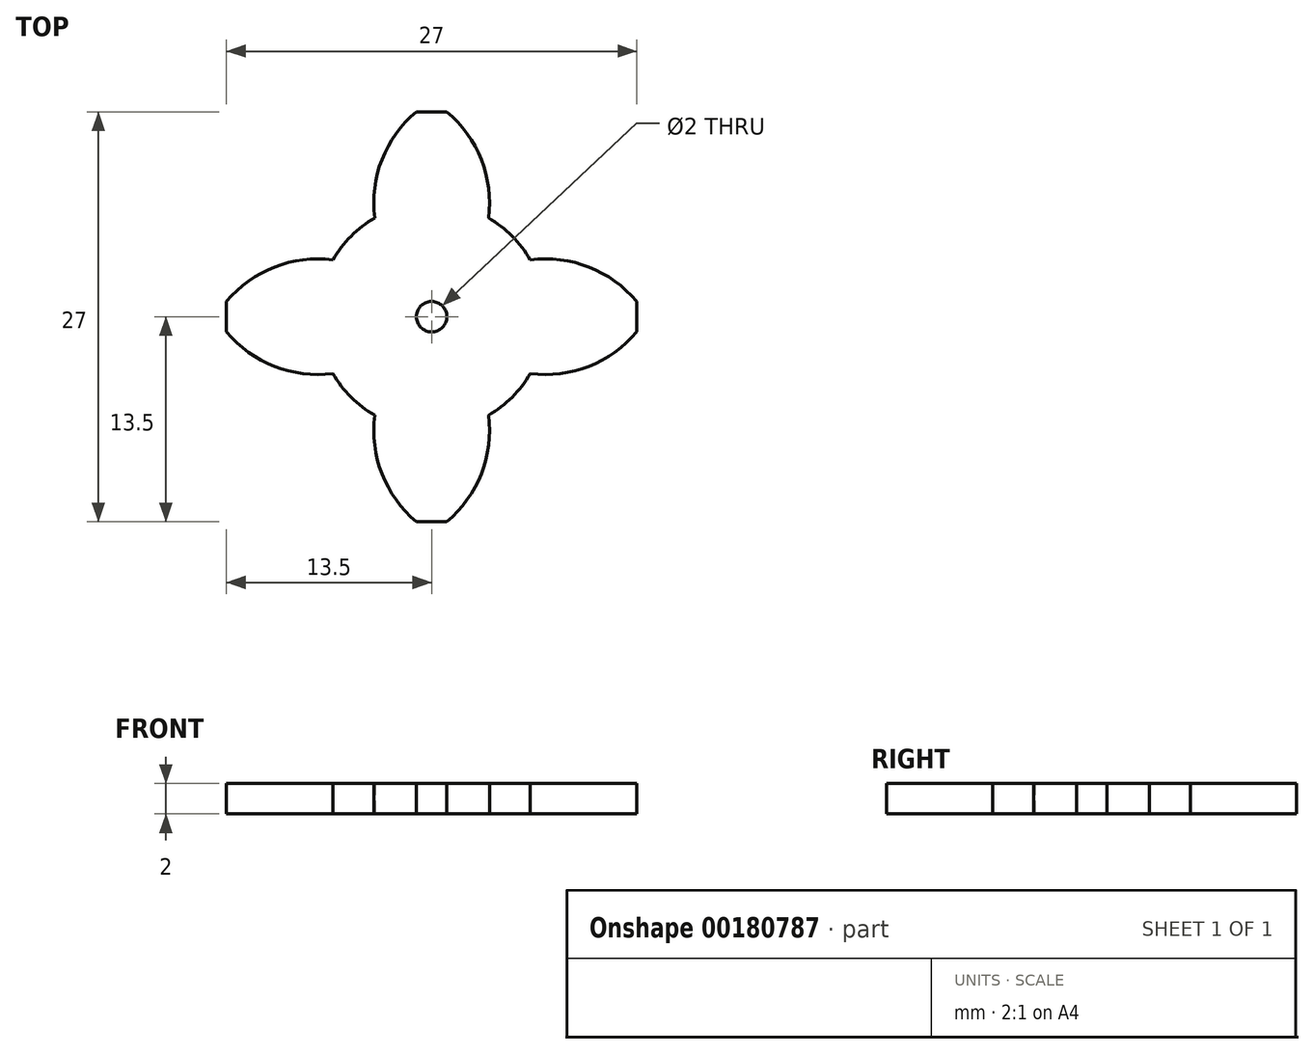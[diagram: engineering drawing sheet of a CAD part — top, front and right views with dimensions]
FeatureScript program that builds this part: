
annotation { "Feature Type Name" : "Feature", "Feature Type Description" : "" }
export const myFeature = defineFeature(function(context is Context, id is Id, definition is map)
    precondition{}
    {
        {
            var Q0;
            Q0=qCreatedBy(makeId("Top.planeOp"),FACE);
            var sketch = newSketch(context, id + "F0", { "sketchPlane" : qUnion([Q0])});
            skCircle(sketch, "E0", {"center": v(0, 0) * mm, "radius": 7.5 * mm});
            skLineSegment(sketch, "E1", {"start": v(0, 0) * mm, "end": v(0, 7.5) * mm, "construction": true});
            skLineSegment(sketch, "E2", {"start": v(0, 7.5) * mm, "end": v(0, 13.5) * mm});
            skLineSegment(sketch, "E3", {"start": v(0, 13.5) * mm, "end": v(-1, 13.5) * mm});
            skArc(sketch, "E4", {"start": v(-1, 13.5) * mm, "mid": v(-3.27, 10.35) * mm, "end": v(-3.75, 6.5) * mm});
            skLineSegment(sketch, "E5.MirrorCS", {"start": v(0, 13.5) * mm, "end": v(1, 13.5) * mm});
            skArc(sketch, "E6.MirrorCS", {"start": v(1, 13.5) * mm, "mid": v(3.27, 10.35) * mm, "end": v(3.75, 6.5) * mm});
            skArc(sketch, "E7.1.0", {"start": v(-13.5, -1) * mm, "mid": v(-10.35, -3.27) * mm, "end": v(-6.5, -3.75) * mm});
            skLineSegment(sketch, "E7.1.1", {"start": v(-13.5, 0) * mm, "end": v(-13.5, -1) * mm});
            skLineSegment(sketch, "E7.1.2", {"start": v(-13.5, 0) * mm, "end": v(-13.5, 1) * mm});
            skArc(sketch, "E7.1.3", {"start": v(-13.5, 1) * mm, "mid": v(-10.35, 3.27) * mm, "end": v(-6.5, 3.75) * mm});
            skArc(sketch, "E7.2.0", {"start": v(1, -13.5) * mm, "mid": v(3.27, -10.35) * mm, "end": v(3.75, -6.5) * mm});
            skLineSegment(sketch, "E7.2.1", {"start": v(0, -13.5) * mm, "end": v(1, -13.5) * mm});
            skLineSegment(sketch, "E7.2.2", {"start": v(0, -13.5) * mm, "end": v(-1, -13.5) * mm});
            skArc(sketch, "E7.2.3", {"start": v(-1, -13.5) * mm, "mid": v(-3.27, -10.35) * mm, "end": v(-3.75, -6.5) * mm});
            skArc(sketch, "E7.3.0", {"start": v(13.5, 1) * mm, "mid": v(10.35, 3.27) * mm, "end": v(6.5, 3.75) * mm});
            skLineSegment(sketch, "E7.3.1", {"start": v(13.5, 0) * mm, "end": v(13.5, 1) * mm});
            skLineSegment(sketch, "E7.3.2", {"start": v(13.5, 0) * mm, "end": v(13.5, -1) * mm});
            skArc(sketch, "E7.3.3", {"start": v(13.5, -1) * mm, "mid": v(10.35, -3.27) * mm, "end": v(6.5, -3.75) * mm});
            skSolve(sketch);
        }
        {
            var Q0;
            Q0 = qSketchRegion(id + "F0", true);
            extrude(context, id + "F1", {"entities" : qUnion([Q0]), "depth" : 2 * mm});
        }
        {
            var Q0;
            Q0=makeQuery(id+"F1.opExtrude","CAP_FACE",FACE,{"disambiguationData":[OSD([sQuery(id+"F0.wireOp",EDGE,"E0"),sQuery(id+"F0.wireOp",EDGE,"E3"),sQuery(id+"F0.wireOp",EDGE,"E4"),sQuery(id+"F0.wireOp",EDGE,"E5.MirrorCS"),sQuery(id+"F0.wireOp",EDGE,"E6.MirrorCS"),sQuery(id+"F0.wireOp",EDGE,"E7.1.0"),sQuery(id+"F0.wireOp",EDGE,"E7.1.1"),sQuery(id+"F0.wireOp",EDGE,"E7.1.2"),sQuery(id+"F0.wireOp",EDGE,"E7.1.3"),sQuery(id+"F0.wireOp",EDGE,"E7.2.0"),sQuery(id+"F0.wireOp",EDGE,"E7.2.1"),sQuery(id+"F0.wireOp",EDGE,"E7.2.2"),sQuery(id+"F0.wireOp",EDGE,"E7.2.3"),sQuery(id+"F0.wireOp",EDGE,"E7.3.0"),sQuery(id+"F0.wireOp",EDGE,"E7.3.1"),sQuery(id+"F0.wireOp",EDGE,"E7.3.2"),sQuery(id+"F0.wireOp",EDGE,"E7.3.3")])],"isStart":false});
            var sketch = newSketch(context, id + "F2", { "sketchPlane" : qUnion([Q0])});
            skCircle(sketch, "E8", {"center": v(0, 0) * mm, "radius": 1 * mm});
            skSolve(sketch);
        }
        {
            var Q0;
            Q0 = qSketchRegion(id + "F2", true);
            extrude(context, id + "F3", {"entities" : qUnion([Q0]), "operationType" : NewBodyOperationType.REMOVE, "endBound" : BoundingType.THROUGH_ALL, "oppositeDirection" : true, "depth" : 25 * mm});
        }
    });
